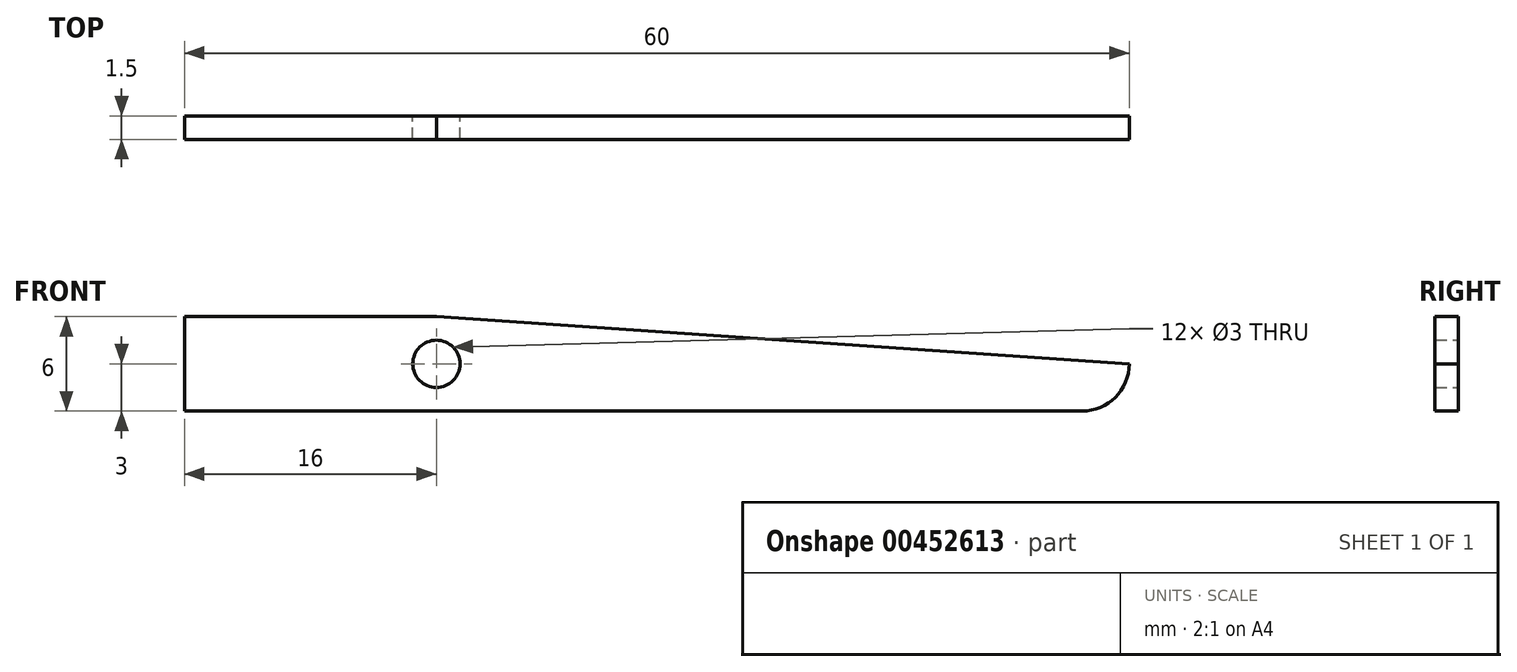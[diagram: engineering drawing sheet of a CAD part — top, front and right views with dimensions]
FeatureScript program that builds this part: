
annotation { "Feature Type Name" : "Feature", "Feature Type Description" : "" }
export const myFeature = defineFeature(function(context is Context, id is Id, definition is map)
    precondition{}
    {
        {
            var Q0;
            Q0=qCreatedBy(makeId("Front.planeOp"),FACE);
            var sketch = newSketch(context, id + "F0", { "sketchPlane" : qUnion([Q0])});
            skCircle(sketch, "E0", {"center": v(0, 0) * mm, "radius": 1.5 * mm});
            skLineSegment(sketch, "E1.bottom", {"start": v(-16, 3) * mm, "end": v(0, 3) * mm});
            skLineSegment(sketch, "E1.top", {"start": v(-16, -3) * mm, "end": v(41, -3) * mm});
            skLineSegment(sketch, "E1.left", {"start": v(-16, 3) * mm, "end": v(-16, -3) * mm});
            skLineSegment(sketch, "E2", {"start": v(0, 0) * mm, "end": v(-16, 0) * mm, "construction": true});
            skPoint(sketch, "E3.visualSharp", {"position": v(48.69, -3) * mm});
            skArc(sketch, "E3.filletArc", {"start": v(41, -3) * mm, "mid": v(43.12, -2.12) * mm, "end": v(44, 0) * mm});
            skPoint(sketch, "E1.right.start.orphan", {"position": v(44, 3) * mm});
            skPoint(sketch, "E4.end.orphan", {"position": v(46.34, 0) * mm});
            skLineSegment(sketch, "E5", {"start": v(0, 3) * mm, "end": v(44, 0) * mm});
            skSolve(sketch);
        }
        {
            var Q0;
            Q0 = qSketchRegion(id + "F0", true);
            extrude(context, id + "F1", {"entities" : qUnion([Q0]), "depth" : 1.5 * mm});
        }
    });
